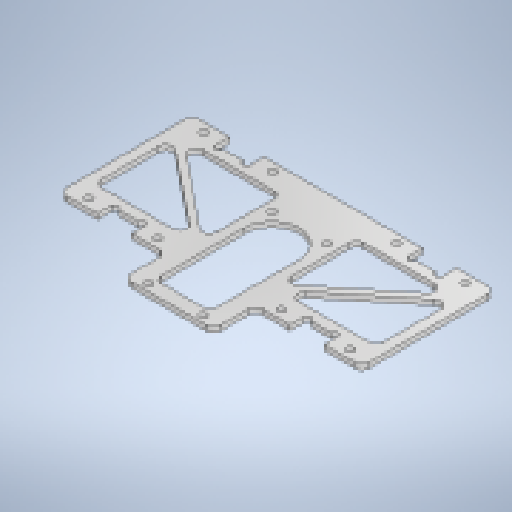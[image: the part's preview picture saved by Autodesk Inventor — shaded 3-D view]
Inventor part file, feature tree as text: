
AUTODESK INVENTOR PART (.ipt)
format: ipt  version: 2025.1 (Build 291241000, 241)  size: 506,880 bytes
history: native  units: mm
features: other x4, extrude x3, fillet x3, reference x1, projected_geometry x1
ambient origin geometry x8: Origin, YZ Plane, XZ Plane, XY Plane, X Axis, Y Axis, Z Axis, Center Point
bodies: Body1 (feature_tree)
feature tree (12):
  other  "ソリッド1"
  extrude  "押し出し1"  Depth=2.2mm
  fillet  "フィレット1"  Radius=16.0mm
  extrude  "押し出し3"  Depth=36.0mm
  fillet  "フィレット2"  Radius=20.0mm
  extrude  "押し出し5"  Depth=20.0mm
  fillet  "フィレット3"  Radius=2.0mm
  other  "スケッチ矩形状パターン1"
  reference  "参照1"
  projected_geometry  "投影ループ1"
  other  "kosi.iam"
  other  "02157_SmallDiameterHornB:1"
